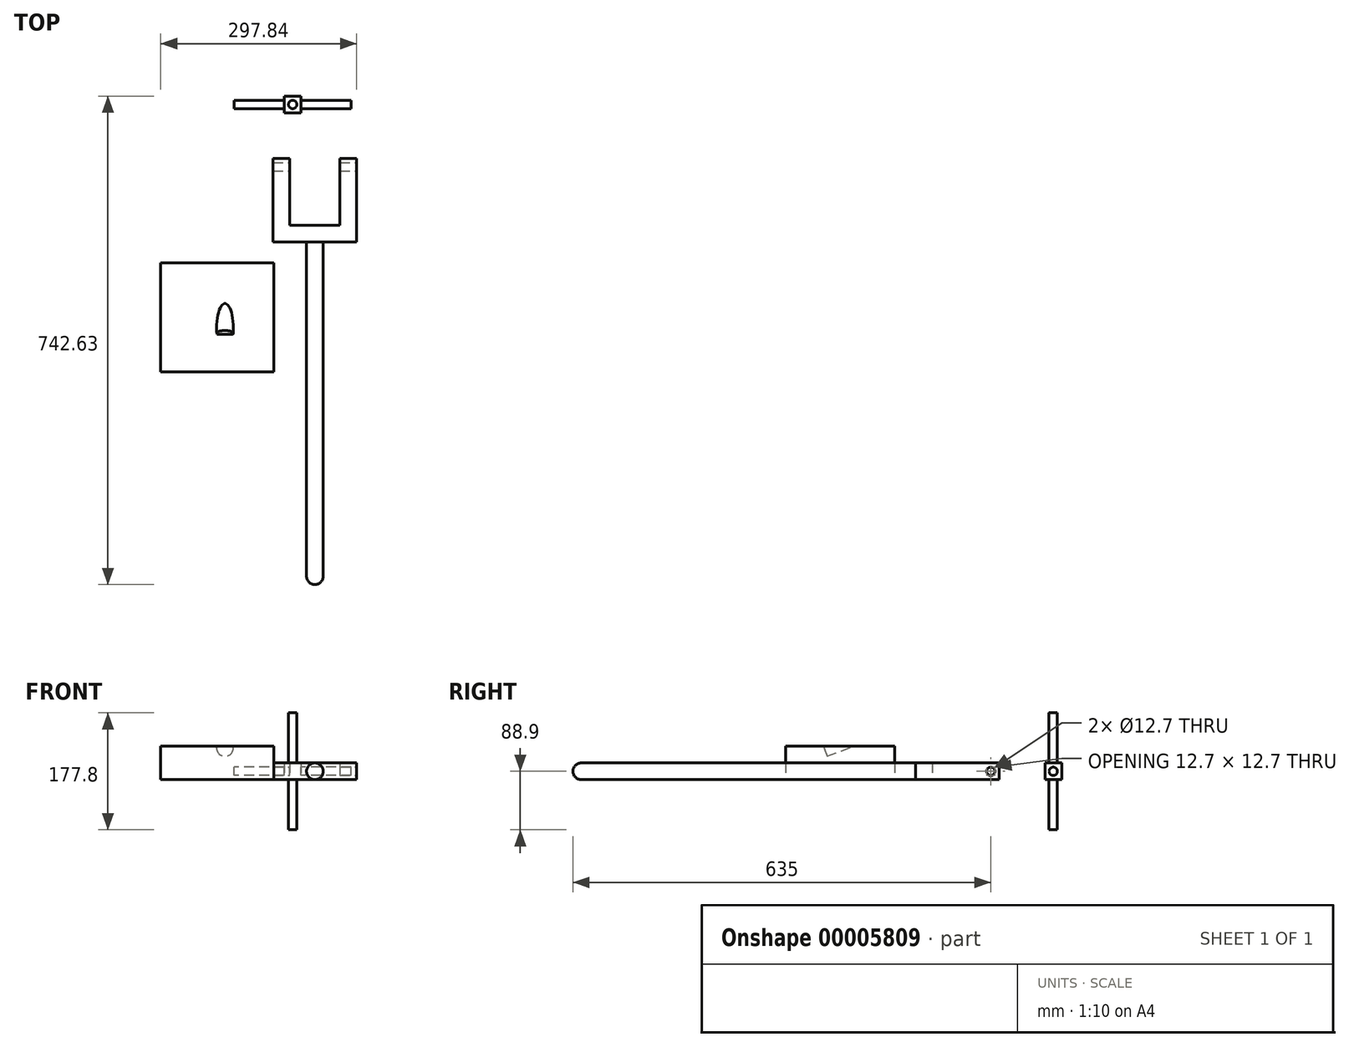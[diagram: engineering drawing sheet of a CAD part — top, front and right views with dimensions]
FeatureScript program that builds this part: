
annotation { "Feature Type Name" : "Feature", "Feature Type Description" : "" }
export const myFeature = defineFeature(function(context is Context, id is Id, definition is map)
    precondition{}
    {
        {
            var Q0;
            Q0=qCreatedBy(makeId("Top.planeOp"),FACE);
            var sketch = newSketch(context, id + "F0", { "sketchPlane" : qUnion([Q0])});
            skLineSegment(sketch, "E0", {"start": v(0, 0) * mm, "end": v(0, -508) * mm});
            skLineSegment(sketch, "E1", {"start": v(25.4, 0) * mm, "end": v(25.4, -508) * mm});
            skArc(sketch, "E2", {"start": v(0, -508) * mm, "mid": v(12.7, -520.7) * mm, "end": v(25.4, -508) * mm});
            skLineSegment(sketch, "E3", {"start": v(0, 0) * mm, "end": v(-50.8, 0) * mm});
            skLineSegment(sketch, "E4", {"start": v(-50.8, 0) * mm, "end": v(-50.8, 127) * mm});
            skLineSegment(sketch, "E5", {"start": v(-50.8, 127) * mm, "end": v(-25.4, 127) * mm});
            skLineSegment(sketch, "E6", {"start": v(-25.4, 127) * mm, "end": v(-25.4, 25.4) * mm});
            skLineSegment(sketch, "E7", {"start": v(-25.4, 25.4) * mm, "end": v(50.8, 25.4) * mm});
            skLineSegment(sketch, "E8", {"start": v(50.8, 25.4) * mm, "end": v(50.8, 127) * mm});
            skLineSegment(sketch, "E9", {"start": v(50.8, 127) * mm, "end": v(76.2, 127) * mm});
            skLineSegment(sketch, "E10", {"start": v(76.2, 127) * mm, "end": v(76.2, 0) * mm});
            skLineSegment(sketch, "E11", {"start": v(76.2, 0) * mm, "end": v(25.4, 0) * mm});
            skSolve(sketch);
        }
        {
            var Q0;
            Q0=makeQuery(id+"F0.imprint","IMPRINT",FACE,{"disambiguationData":[TD([[makeQuery(id+"F0.imprint","IMPRINT",EDGE,{"derivedFrom":sQuery(id+"F0.wireOp",EDGE,"E0")}),1.0]])]});
            extrude(context, id + "F1", {"entities" : qUnion([Q0]), "depth" : 25.4 * mm});
        }
        {
            var Q0;
            Q0=makeQuery(id+"F1.opExtrude","CAP_EDGE",EDGE,{"disambiguationData":[OSD([sQuery(id+"F0.wireOp",EDGE,"E1")])],"isStart":false});
            var Q1;
            Q1=makeQuery(id+"F1.opExtrude","CAP_EDGE",EDGE,{"disambiguationData":[OSD([sQuery(id+"F0.wireOp",EDGE,"E1")])],"isStart":true});
            var Q2;
            Q2=makeQuery(id+"F1.opExtrude","CAP_EDGE",EDGE,{"disambiguationData":[OSD([sQuery(id+"F0.wireOp",EDGE,"E0")])],"isStart":true});
            var Q3;
            Q3=makeQuery(id+"F1.opExtrude","CAP_EDGE",EDGE,{"disambiguationData":[OSD([sQuery(id+"F0.wireOp",EDGE,"E0")])],"isStart":false});
            fillet(context, id + "F2", {"entities" : qUnion([Q0, Q1, Q2, Q3]), "radius" : 12.7 * mm, "tangentPropagation" : true, "allowEdgeOverflow" : false});
        }
        {
            var Q0;
            Q0=makeQuery(id+"F1.opExtrude","SWEPT_FACE",FACE,{"disambiguationData":[OSD([sQuery(id+"F0.wireOp",EDGE,"E6")])]});
            var sketch = newSketch(context, id + "F3", { "sketchPlane" : qUnion([Q0])});
            skCircle(sketch, "E12", {"center": v(114.3, 12.7) * mm, "radius": 6.35 * mm});
            skSolve(sketch);
        }
        {
            var Q0;
            Q0=makeQuery(id+"F3.imprint","IMPRINT",FACE,{"disambiguationData":[TD([[makeQuery(id+"F3.imprint","IMPRINT",EDGE,{"derivedFrom":sQuery(id+"F3.wireOp",EDGE,"E12")}),1.0]])]});
            extrude(context, id + "F4", {"entities" : qUnion([Q0]), "operationType" : NewBodyOperationType.REMOVE, "endBound" : BoundingType.THROUGH_ALL, "oppositeDirection" : true, "depth" : 25.4 * mm, "hasSecondDirection" : true, "secondDirectionBound" : SecondDirectionBoundingType.THROUGH_ALL, "secondDirectionOppositeDirection" : false, "secondDirectionDepth" : 25.4 * mm});
        }
        {
            var Q0;
            Q0=qCreatedBy(makeId("Top.planeOp"),FACE);
            var sketch = newSketch(context, id + "F5", { "sketchPlane" : qUnion([Q0])});
            skLineSegment(sketch, "E13.rect.bottom", {"start": v(-8.26, 221.93) * mm, "end": v(-33.66, 221.93) * mm});
            skLineSegment(sketch, "E13.rect.top", {"start": v(-8.26, 196.53) * mm, "end": v(-33.66, 196.53) * mm});
            skLineSegment(sketch, "E13.rect.left", {"start": v(-8.26, 221.93) * mm, "end": v(-8.26, 196.53) * mm});
            skLineSegment(sketch, "E13.rect.right", {"start": v(-33.66, 221.93) * mm, "end": v(-33.66, 196.53) * mm});
            skPoint(sketch, "E13.rect.middle", {"position": v(-20.96, 209.23) * mm});
            skSolve(sketch);
        }
        {
            var Q0;
            Q0=makeQuery(id+"F5.imprint","IMPRINT",FACE,{"disambiguationData":[TD([[makeQuery(id+"F5.imprint","IMPRINT",EDGE,{"derivedFrom":sQuery(id+"F5.wireOp",EDGE,"E13.rect.bottom")}),1.0]])]});
            extrude(context, id + "F6", {"entities" : qUnion([Q0]), "depth" : 25.4 * mm});
        }
        {
            var Q0;
            Q0=makeQuery(id+"F6.opExtrude","SWEPT_FACE",FACE,{"disambiguationData":[OSD([sQuery(id+"F5.wireOp",EDGE,"E13.rect.left")])]});
            var sketch = newSketch(context, id + "F7", { "sketchPlane" : qUnion([Q0])});
            skCircle(sketch, "E14", {"center": v(209.23, 12.7) * mm, "radius": 6.35 * mm});
            skSolve(sketch);
        }
        {
            var Q0;
            Q0=makeQuery(id+"F7.imprint","IMPRINT",FACE,{"disambiguationData":[TD([[makeQuery(id+"F7.imprint","IMPRINT",EDGE,{"derivedFrom":sQuery(id+"F7.wireOp",EDGE,"E14")}),1.0]])]});
            extrude(context, id + "F8", {"entities" : qUnion([Q0]), "operationType" : NewBodyOperationType.ADD, "depth" : 76.2 * mm, "hasSecondDirection" : true, "secondDirectionOppositeDirection" : true, "secondDirectionDepth" : 101.6 * mm});
        }
        {
            var Q0;
            Q0=makeQuery(id+"F6.opExtrude","CAP_FACE",FACE,{"disambiguationData":[OSD([sQuery(id+"F5.wireOp",EDGE,"E13.rect.bottom"),sQuery(id+"F5.wireOp",EDGE,"E13.rect.top"),sQuery(id+"F5.wireOp",EDGE,"E13.rect.left"),sQuery(id+"F5.wireOp",EDGE,"E13.rect.right")])],"isStart":false});
            var sketch = newSketch(context, id + "F9", { "sketchPlane" : qUnion([Q0])});
            skCircle(sketch, "E15", {"center": v(-20.96, 209.23) * mm, "radius": 6.35 * mm});
            skSolve(sketch);
        }
        {
            var Q0;
            Q0=makeQuery(id+"F9.imprint","IMPRINT",FACE,{"disambiguationData":[TD([[makeQuery(id+"F9.imprint","IMPRINT",EDGE,{"derivedFrom":sQuery(id+"F9.wireOp",EDGE,"E15")}),1.0]])]});
            extrude(context, id + "F10", {"entities" : qUnion([Q0]), "operationType" : NewBodyOperationType.ADD, "depth" : 76.2 * mm, "hasSecondDirection" : true, "secondDirectionOppositeDirection" : true, "secondDirectionDepth" : 101.6 * mm});
        }
        {
            var Q0;
            Q0=qCreatedBy(makeId("Top.planeOp"),FACE);
            var sketch = newSketch(context, id + "F11", { "sketchPlane" : qUnion([Q0])});
            skLineSegment(sketch, "E16.bottom", {"start": v(-49.48, -31.79) * mm, "end": v(-221.64, -31.79) * mm});
            skLineSegment(sketch, "E16.top", {"start": v(-49.48, -197.4) * mm, "end": v(-221.64, -197.4) * mm});
            skLineSegment(sketch, "E16.left", {"start": v(-49.48, -31.79) * mm, "end": v(-49.48, -197.4) * mm});
            skLineSegment(sketch, "E16.right", {"start": v(-221.64, -31.79) * mm, "end": v(-221.64, -197.4) * mm});
            skSolve(sketch);
        }
        {
            var Q0;
            Q0=makeQuery(id+"F11.imprint","IMPRINT",FACE,{"disambiguationData":[TD([[makeQuery(id+"F11.imprint","IMPRINT",EDGE,{"derivedFrom":sQuery(id+"F11.wireOp",EDGE,"E16.bottom")}),1.0]])]});
            extrude(context, id + "F12", {"entities" : qUnion([Q0]), "depth" : 50.8 * mm});
        }
        {
            var Q0;
            Q0=makeQuery(id+"F12.opExtrude","CAP_EDGE",EDGE,{"disambiguationData":[OSD([sQuery(id+"F11.wireOp",EDGE,"E16.bottom")])],"isStart":false});
            cPlane(context, id + "F13", {"entities" : qUnion([Q0]), "cplaneType" : CPlaneType.LINE_ANGLE, "offset" : 152.4 * mm, "angle" : 340 * degree, "width" : 152.4 * mm, "height" : 152.4 * mm});
        }
        {
            var Q0;
            Q0=qCreatedBy(id+"F13.planeOp",FACE);
            var sketch = newSketch(context, id + "F14", { "sketchPlane" : qUnion([Q0])});
            skCircle(sketch, "E17", {"center": v(-123.89, 92.36) * mm, "radius": 12.7 * mm});
            skSolve(sketch);
        }
        {
            var Q0;
            Q0=makeQuery(id+"F14.imprint","IMPRINT",FACE,{"disambiguationData":[TD([[makeQuery(id+"F14.imprint","IMPRINT",EDGE,{"derivedFrom":sQuery(id+"F14.wireOp",EDGE,"E17")}),1.0]])]});
            extrude(context, id + "F15", {"entities" : qUnion([Q0]), "operationType" : NewBodyOperationType.REMOVE, "depth" : 101.6 * mm});
        }
    });
